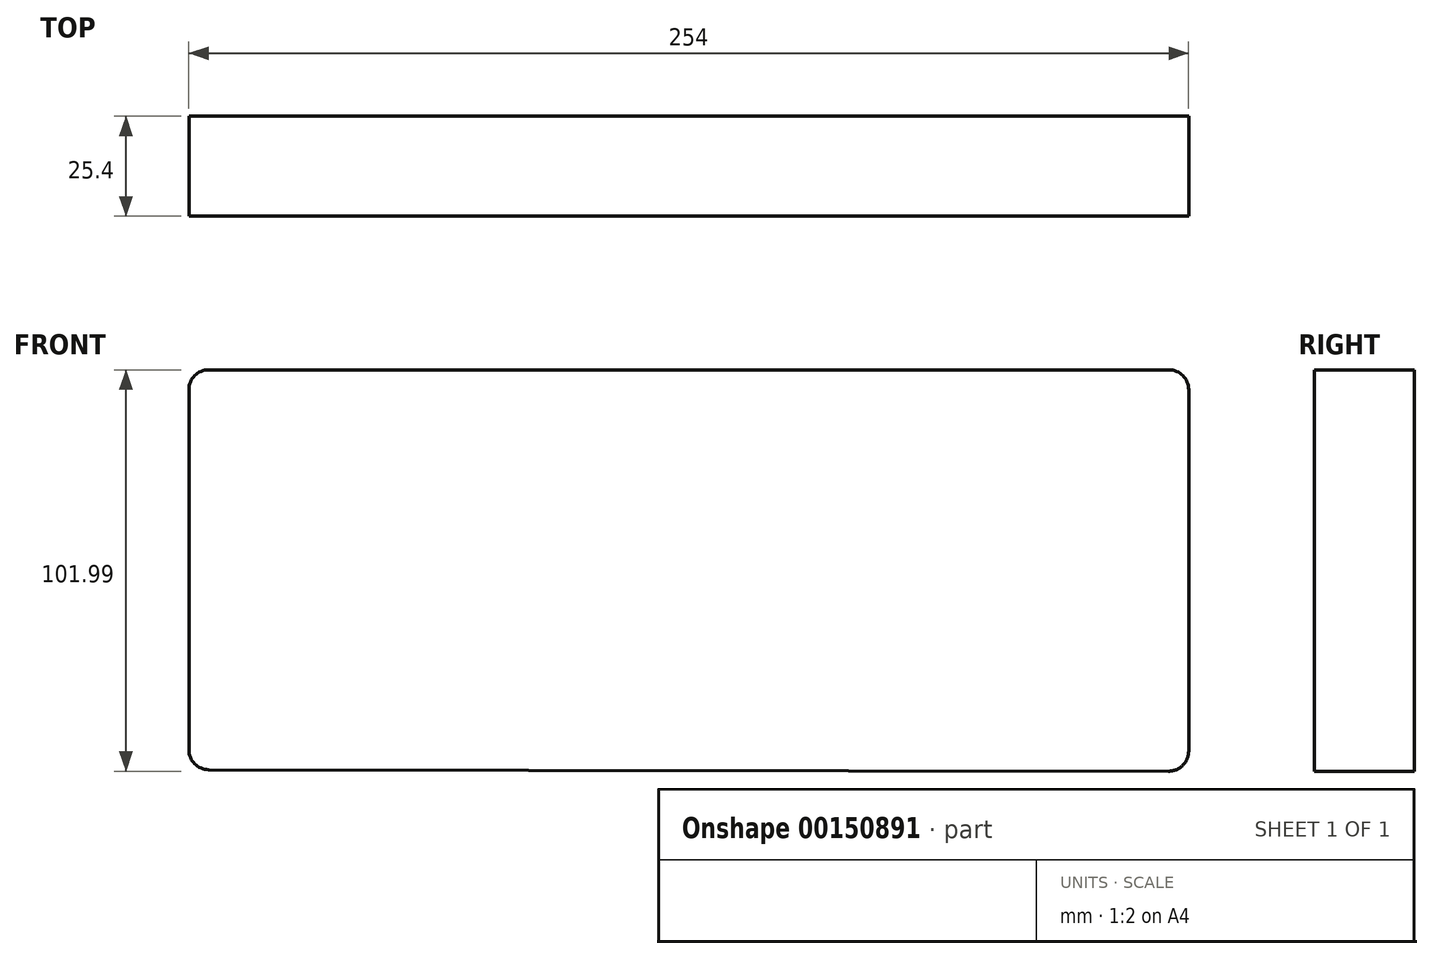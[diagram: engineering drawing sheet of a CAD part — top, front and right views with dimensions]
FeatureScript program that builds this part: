
annotation { "Feature Type Name" : "Feature", "Feature Type Description" : "" }
export const myFeature = defineFeature(function(context is Context, id is Id, definition is map)
    precondition{}
    {
        {
            var Q0;
            Q0=qCreatedBy(makeId("Front.planeOp"),FACE);
            var sketch = newSketch(context, id + "F0", { "sketchPlane" : qUnion([Q0])});
            skLineSegment(sketch, "E0", {"start": v(-135.24, 37.12) * mm, "end": v(-135.24, -64.48) * mm});
            skLineSegment(sketch, "E1", {"start": v(-135.24, 37.12) * mm, "end": v(118.76, 37.12) * mm});
            skLineSegment(sketch, "E2", {"start": v(118.76, 37.12) * mm, "end": v(118.76, -64.88) * mm});
            skLineSegment(sketch, "E3", {"start": v(118.76, -64.88) * mm, "end": v(-135.24, -64.48) * mm});
            skSolve(sketch);
        }
        {
            var Q0;
            Q0 = qSketchRegion(id + "F0", true);
            extrude(context, id + "F1", {"entities" : qUnion([Q0]), "depth" : 25.4 * mm});
        }
        {
            var Q0;
            Q0=makeQuery(id+"F1.opExtrude","SWEPT_EDGE",EDGE,{"disambiguationData":[OSD([sQuery(id+"F0.wireOp",EDGE,"E0"),sQuery(id+"F0.wireOp",EDGE,"E1")])]});
            fillet(context, id + "F2", {"entities" : qUnion([Q0]), "radius" : 5.08 * mm, "tangentPropagation" : true, "allowEdgeOverflow" : false});
        }
        {
            var Q0;
            Q0=makeQuery(id+"F1.opExtrude","SWEPT_EDGE",EDGE,{"disambiguationData":[OSD([sQuery(id+"F0.wireOp",EDGE,"E1"),sQuery(id+"F0.wireOp",EDGE,"E2")])]});
            var Q1;
            Q1=makeQuery(id+"F1.opExtrude","SWEPT_EDGE",EDGE,{"disambiguationData":[OSD([sQuery(id+"F0.wireOp",EDGE,"E2"),sQuery(id+"F0.wireOp",EDGE,"E3")])]});
            var Q2;
            Q2=makeQuery(id+"F1.opExtrude","SWEPT_EDGE",EDGE,{"disambiguationData":[OSD([sQuery(id+"F0.wireOp",EDGE,"E0"),sQuery(id+"F0.wireOp",EDGE,"E3")])]});
            fillet(context, id + "F3", {"entities" : qUnion([Q0, Q1, Q2]), "radius" : 5.08 * mm, "tangentPropagation" : true, "allowEdgeOverflow" : false});
        }
    });
